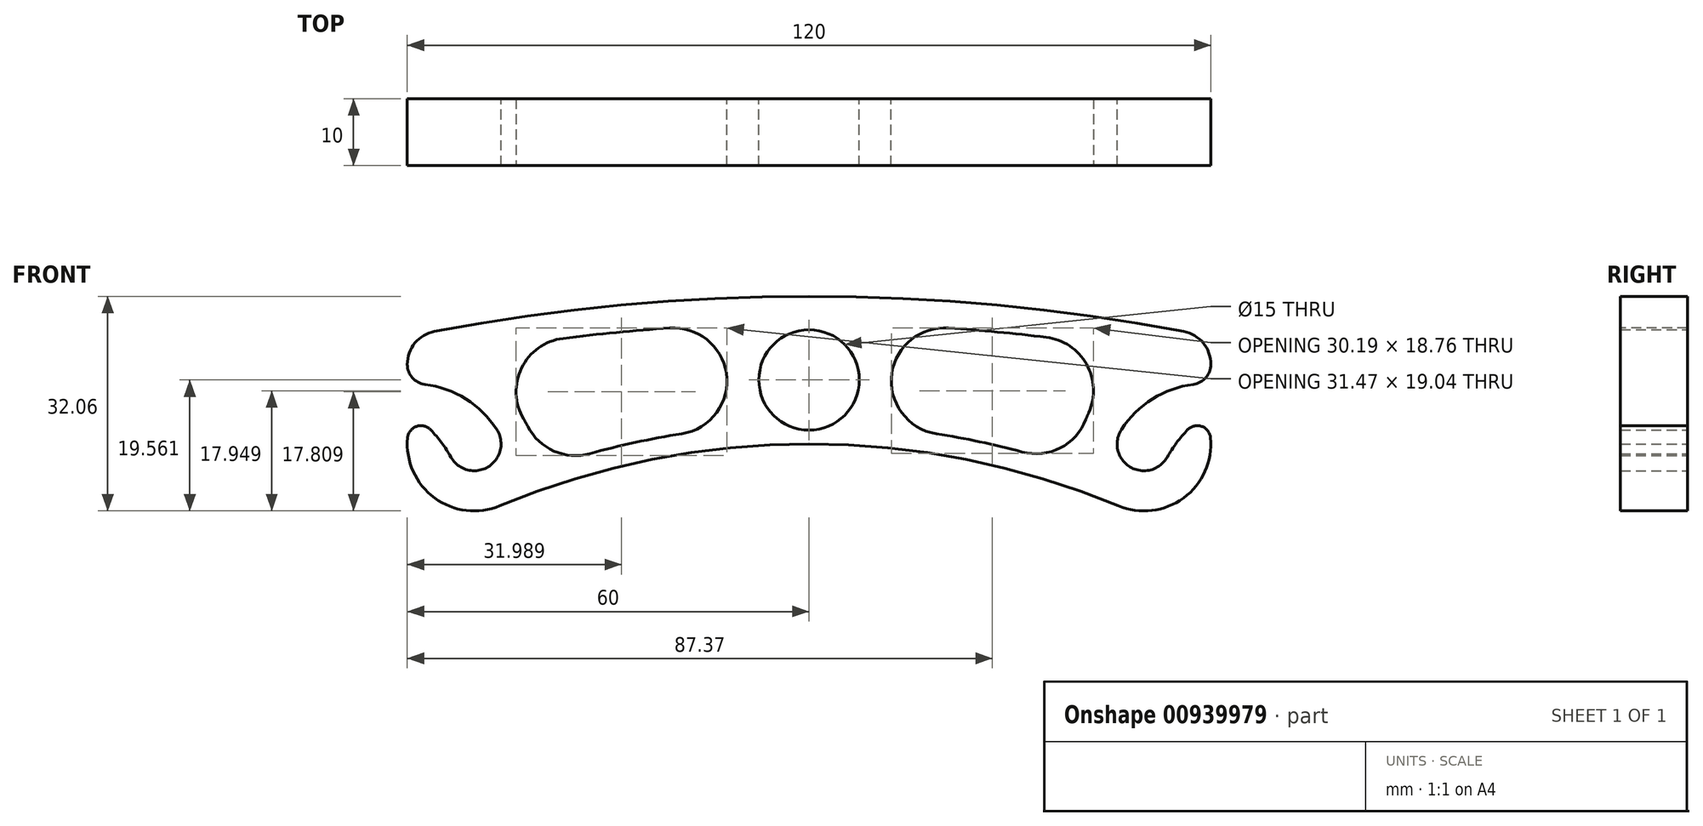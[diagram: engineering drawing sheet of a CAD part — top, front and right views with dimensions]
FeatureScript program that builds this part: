
annotation { "Feature Type Name" : "Feature", "Feature Type Description" : "" }
export const myFeature = defineFeature(function(context is Context, id is Id, definition is map)
    precondition{}
    {
        {
            var Q0;
            Q0=qCreatedBy(makeId("Front.planeOp"),FACE);
            var sketch = newSketch(context, id + "F0", { "sketchPlane" : qUnion([Q0])});
            skCircle(sketch, "E0", {"center": v(-50, 0) * mm, "radius": 4 * mm});
            skCircle(sketch, "E1", {"center": v(-50, 0) * mm, "radius": 10 * mm});
            skCircle(sketch, "E2", {"center": v(50, 0) * mm, "radius": 4 * mm});
            skCircle(sketch, "E3", {"center": v(50, 0) * mm, "radius": 10 * mm});
            skCircle(sketch, "E4", {"center": v(0, 9.56) * mm, "radius": 7.5 * mm});
            skArc(sketch, "E5", {"start": v(46.15, -9.23) * mm, "mid": v(0, 0) * mm, "end": v(-46.15, -9.23) * mm});
            skLineSegment(sketch, "E6", {"start": v(-60, 0) * mm, "end": v(-60, 16) * mm});
            skLineSegment(sketch, "E7", {"start": v(60, 16) * mm, "end": v(60, 0) * mm});
            skArc(sketch, "E8", {"start": v(-53.49, -1.96) * mm, "mid": v(-56.32, 1.91) * mm, "end": v(-60, 5) * mm});
            skArc(sketch, "E9", {"start": v(-46.64, 2.17) * mm, "mid": v(-52.4, 7.38) * mm, "end": v(-60, 9) * mm});
            skLineSegment(sketch, "E10", {"start": v(0, 22.06) * mm, "end": v(0, 0) * mm});
            skArc(sketch, "E11", {"start": v(-4, -0.07) * mm, "mid": v(-4.63, 2.62) * mm, "end": v(-5.98, 5.04) * mm});
            skArc(sketch, "E12", {"start": v(60, 16) * mm, "mid": v(0, 22.06) * mm, "end": v(-60, 16) * mm});
            skSolve(sketch);
        }
        {
            var Q0;
            {var subQ5=sQuery(id+"F0.wireOp",EDGE,"E11");Q0=makeQuery(id+"F0.imprint","IMPRINT",FACE,{"disambiguationData":[TD([[makeQuery(id+"F0.imprint","IMPRINT",EDGE,{"derivedFrom":subQ5}),1.0]])]});}
            var Q1;
            {var subQ5=sQuery(id+"F0.wireOp",EDGE,"E8");var subQ7=sQuery(id+"F0.wireOp",EDGE,"E0");var subQ8=makeQuery(id+"F0.imprint","INTERSECT",VERTEX,{"derivedFrom":[subQ7,subQ5]});Q1=makeQuery(id+"F0.imprint","IMPRINT",FACE,{"disambiguationData":[TD([[makeQuery(id+"F0.imprint","IMPRINT",EDGE,{"disambiguationData":[TD([[subQ8,-1.0]])],"derivedFrom":subQ7}),-1.0]])]});}
            var Q2;
            {var subQ0=sQuery(id+"F0.wireOp",EDGE,"E11");Q2=makeQuery(id+"F0.imprint","IMPRINT",FACE,{"disambiguationData":[TD([[makeQuery(id+"F0.imprint","IMPRINT",EDGE,{"derivedFrom":subQ0}),-1.0]])]});}
            extrude(context, id + "F1", {"entities" : qUnion([Q0, Q1, Q2]), "depth" : 10 * mm, "offsetDistance" : 25 * mm});
        }
        {
            var Q0;
            Q0=makeQuery(id+"F1.opExtrude","SWEPT_BODY",BODY,{"disambiguationData":[OSD([sQuery(id+"F0.wireOp",EDGE,"E0"),sQuery(id+"F0.wireOp",EDGE,"E1"),sQuery(id+"F0.wireOp",EDGE,"E4"),sQuery(id+"F0.wireOp",EDGE,"E5"),sQuery(id+"F0.wireOp",EDGE,"E6"),sQuery(id+"F0.wireOp",EDGE,"80QlOabB-7I2Q-YexZ-uaV2-opwIIh4Y06iD"),sQuery(id+"F0.wireOp",EDGE,"E8"),sQuery(id+"F0.wireOp",EDGE,"E9"),sQuery(id+"F0.wireOp",EDGE,"E10"),sQuery(id+"F0.wireOp",EDGE,"E11")])]});
            var Q1;
            Q1=qCreatedBy(makeId("Right.planeOp"),FACE);
            mirror(context, id + "F2", {"operationType" : NewBodyOperationType.ADD, "entities" : qUnion([Q0]), "mirrorPlane" : qUnion([Q1])});
        }
        {
            var Q0;
            Q0=makeQuery(id+"F1.opExtrude","SWEPT_EDGE",EDGE,{"disambiguationData":[OSD([sQuery(id+"F0.wireOp",EDGE,"E6"),sQuery(id+"F0.wireOp",EDGE,"E12")])]});
            var Q1;
            Q1=makeQuery(id+"F2.opPattern","COPY",EDGE,{"derivedFrom":makeQuery(id+"F1.opExtrude","SWEPT_EDGE",EDGE,{"disambiguationData":[OSD([sQuery(id+"F0.wireOp",EDGE,"E6"),sQuery(id+"F0.wireOp",EDGE,"E12")])]}),"instanceName":"1"});
            fillet(context, id + "F3", {"entities" : qUnion([Q0, Q1]), "radius" : 5 * mm, "tangentPropagation" : true, "allowEdgeOverflow" : false});
        }
        {
            var Q0;
            Q0=makeQuery(id+"F1.opExtrude","SWEPT_EDGE",EDGE,{"disambiguationData":[OSD([sQuery(id+"F0.wireOp",EDGE,"E6"),sQuery(id+"F0.wireOp",EDGE,"E9")])]});
            var Q1;
            Q1=makeQuery(id+"F2.opPattern","COPY",EDGE,{"derivedFrom":makeQuery(id+"F1.opExtrude","SWEPT_EDGE",EDGE,{"disambiguationData":[OSD([sQuery(id+"F0.wireOp",EDGE,"E6"),sQuery(id+"F0.wireOp",EDGE,"E9")])]}),"instanceName":"1"});
            fillet(context, id + "F4", {"entities" : qUnion([Q0, Q1]), "radius" : 3 * mm, "tangentPropagation" : true, "allowEdgeOverflow" : false});
        }
        {
            var Q0;
            Q0=makeQuery(id+"F1.opExtrude","SWEPT_EDGE",EDGE,{"disambiguationData":[OSD([sQuery(id+"F0.wireOp",EDGE,"E1"),sQuery(id+"F0.wireOp",EDGE,"E8")])]});
            var Q1;
            Q1=makeQuery(id+"F2.opPattern","COPY",EDGE,{"derivedFrom":makeQuery(id+"F1.opExtrude","SWEPT_EDGE",EDGE,{"disambiguationData":[OSD([sQuery(id+"F0.wireOp",EDGE,"E1"),sQuery(id+"F0.wireOp",EDGE,"E8")])]}),"instanceName":"1"});
            fillet(context, id + "F5", {"entities" : qUnion([Q0, Q1]), "radius" : 2 * mm, "tangentPropagation" : true, "allowEdgeOverflow" : false});
        }
        {
            var Q0;
            {var subQ0=makeQuery(id+"F1.opExtrude","CAP_FACE",FACE,{"disambiguationData":[OSD([sQuery(id+"F0.wireOp",EDGE,"E0"),sQuery(id+"F0.wireOp",EDGE,"E1"),sQuery(id+"F0.wireOp",EDGE,"E4"),sQuery(id+"F0.wireOp",EDGE,"E5"),sQuery(id+"F0.wireOp",EDGE,"E6"),sQuery(id+"F0.wireOp",EDGE,"E8"),sQuery(id+"F0.wireOp",EDGE,"E9"),sQuery(id+"F0.wireOp",EDGE,"E10"),sQuery(id+"F0.wireOp",EDGE,"E12")])],"isStart":false});Q0=makeQuery(id+"F2.boolean.opBoolean","MERGE",FACE,{"derivedFrom":[subQ0,makeQuery(id+"F2.opPattern","COPY",FACE,{"derivedFrom":subQ0,"instanceName":"1"})]});}
            var sketch = newSketch(context, id + "F6", { "sketchPlane" : qUnion([Q0])});
            skArc(sketch, "E13.4", {"start": v(50, 13.8) * mm, "mid": v(-2.54, 18.05) * mm, "end": v(-55, 12.9) * mm});
            skArc(sketch, "E14", {"start": v(40, -3.69) * mm, "mid": v(0, 3) * mm, "end": v(-40, -3.69) * mm});
            skCircle(sketch, "E15", {"center": v(0, 12.5) * mm, "radius": 12.5 * mm});
            skArc(sketch, "E16", {"start": v(-40, -3.69) * mm, "mid": v(-44.96, 6.9) * mm, "end": v(-55, 12.9) * mm});
            skArc(sketch, "E17", {"start": v(50, 13.8) * mm, "mid": v(42.64, 6.41) * mm, "end": v(40, -3.69) * mm});
            skSolve(sketch);
        }
        {
            var Q0;
            {var subQ0=sQuery(id+"F6.wireOp",EDGE,"E16");Q0=makeQuery(id+"F6.imprint","IMPRINT",FACE,{"disambiguationData":[TD([[makeQuery(id+"F6.imprint","IMPRINT",EDGE,{"derivedFrom":subQ0}),-1.0]])]});}
            var Q1;
            {var subQ0=sQuery(id+"F6.wireOp",EDGE,"E17");Q1=makeQuery(id+"F6.imprint","IMPRINT",FACE,{"disambiguationData":[TD([[makeQuery(id+"F6.imprint","IMPRINT",EDGE,{"derivedFrom":subQ0}),-1.0]])]});}
            extrude(context, id + "F7", {"entities" : qUnion([Q0, Q1]), "operationType" : NewBodyOperationType.REMOVE, "endBound" : BoundingType.THROUGH_ALL, "oppositeDirection" : true, "depth" : 25 * mm, "offsetDistance" : 25 * mm});
        }
        {
            var Q0;
            Q0=makeQuery(id+"F7.boolean.opBoolean","COPY",EDGE,{"derivedFrom":makeQuery(id+"F7.opExtrude","SWEPT_EDGE",EDGE,{"disambiguationData":[OSD([sQuery(id+"F6.wireOp",EDGE,"E13.4"),sQuery(id+"F6.wireOp",EDGE,"E16")])]})});
            var Q1;
            Q1=makeQuery(id+"F7.boolean.opBoolean","COPY",EDGE,{"derivedFrom":makeQuery(id+"F7.opExtrude","SWEPT_EDGE",EDGE,{"disambiguationData":[OSD([sQuery(id+"F6.wireOp",EDGE,"E14"),sQuery(id+"F6.wireOp",EDGE,"E16")])]})});
            var Q2;
            {var subQ0=sQuery(id+"F6.wireOp",EDGE,"E15");var subQ1=sQuery(id+"F6.wireOp",EDGE,"E14");Q2=makeQuery(id+"F7.boolean.opBoolean","COPY",EDGE,{"derivedFrom":makeQuery(id+"F7.opExtrude","SWEPT_EDGE",EDGE,{"disambiguationData":[OSD([subQ1,subQ0]),TDD([makeQuery(id+"F6.imprint","INTERSECT",VERTEX,{"disambiguationData":[OD(1.0)],"derivedFrom":[subQ1,subQ0]})])]})});}
            var Q3;
            {var subQ0=sQuery(id+"F6.wireOp",EDGE,"E15");var subQ1=sQuery(id+"F6.wireOp",EDGE,"E13.4");Q3=makeQuery(id+"F7.boolean.opBoolean","COPY",EDGE,{"derivedFrom":makeQuery(id+"F7.opExtrude","SWEPT_EDGE",EDGE,{"disambiguationData":[OSD([subQ1,subQ0]),TDD([makeQuery(id+"F6.imprint","INTERSECT",VERTEX,{"disambiguationData":[OD(1.0)],"derivedFrom":[subQ1,subQ0]})])]})});}
            var Q4;
            {var subQ0=sQuery(id+"F6.wireOp",EDGE,"E15");var subQ1=sQuery(id+"F6.wireOp",EDGE,"E13.4");Q4=makeQuery(id+"F7.boolean.opBoolean","COPY",EDGE,{"derivedFrom":makeQuery(id+"F7.opExtrude","SWEPT_EDGE",EDGE,{"disambiguationData":[OSD([subQ1,subQ0]),TDD([makeQuery(id+"F6.imprint","INTERSECT",VERTEX,{"disambiguationData":[OD(0.0)],"derivedFrom":[subQ1,subQ0]})])]})});}
            var Q5;
            {var subQ0=sQuery(id+"F6.wireOp",EDGE,"E15");var subQ1=sQuery(id+"F6.wireOp",EDGE,"E14");Q5=makeQuery(id+"F7.boolean.opBoolean","COPY",EDGE,{"derivedFrom":makeQuery(id+"F7.opExtrude","SWEPT_EDGE",EDGE,{"disambiguationData":[OSD([subQ1,subQ0]),TDD([makeQuery(id+"F6.imprint","INTERSECT",VERTEX,{"disambiguationData":[OD(0.0)],"derivedFrom":[subQ1,subQ0]})])]})});}
            var Q6;
            Q6=makeQuery(id+"F7.boolean.opBoolean","COPY",EDGE,{"derivedFrom":makeQuery(id+"F7.opExtrude","SWEPT_EDGE",EDGE,{"disambiguationData":[OSD([sQuery(id+"F6.wireOp",EDGE,"E13.4"),sQuery(id+"F6.wireOp",EDGE,"E17")])]})});
            var Q7;
            Q7=makeQuery(id+"F7.boolean.opBoolean","COPY",EDGE,{"derivedFrom":makeQuery(id+"F7.opExtrude","SWEPT_EDGE",EDGE,{"disambiguationData":[OSD([sQuery(id+"F6.wireOp",EDGE,"E14"),sQuery(id+"F6.wireOp",EDGE,"E17")])]})});
            fillet(context, id + "F8", {"entities" : qUnion([Q0, Q1, Q2, Q3, Q4, Q5, Q6, Q7]), "radius" : 8 * mm, "tangentPropagation" : true, "allowEdgeOverflow" : false});
        }
    });
